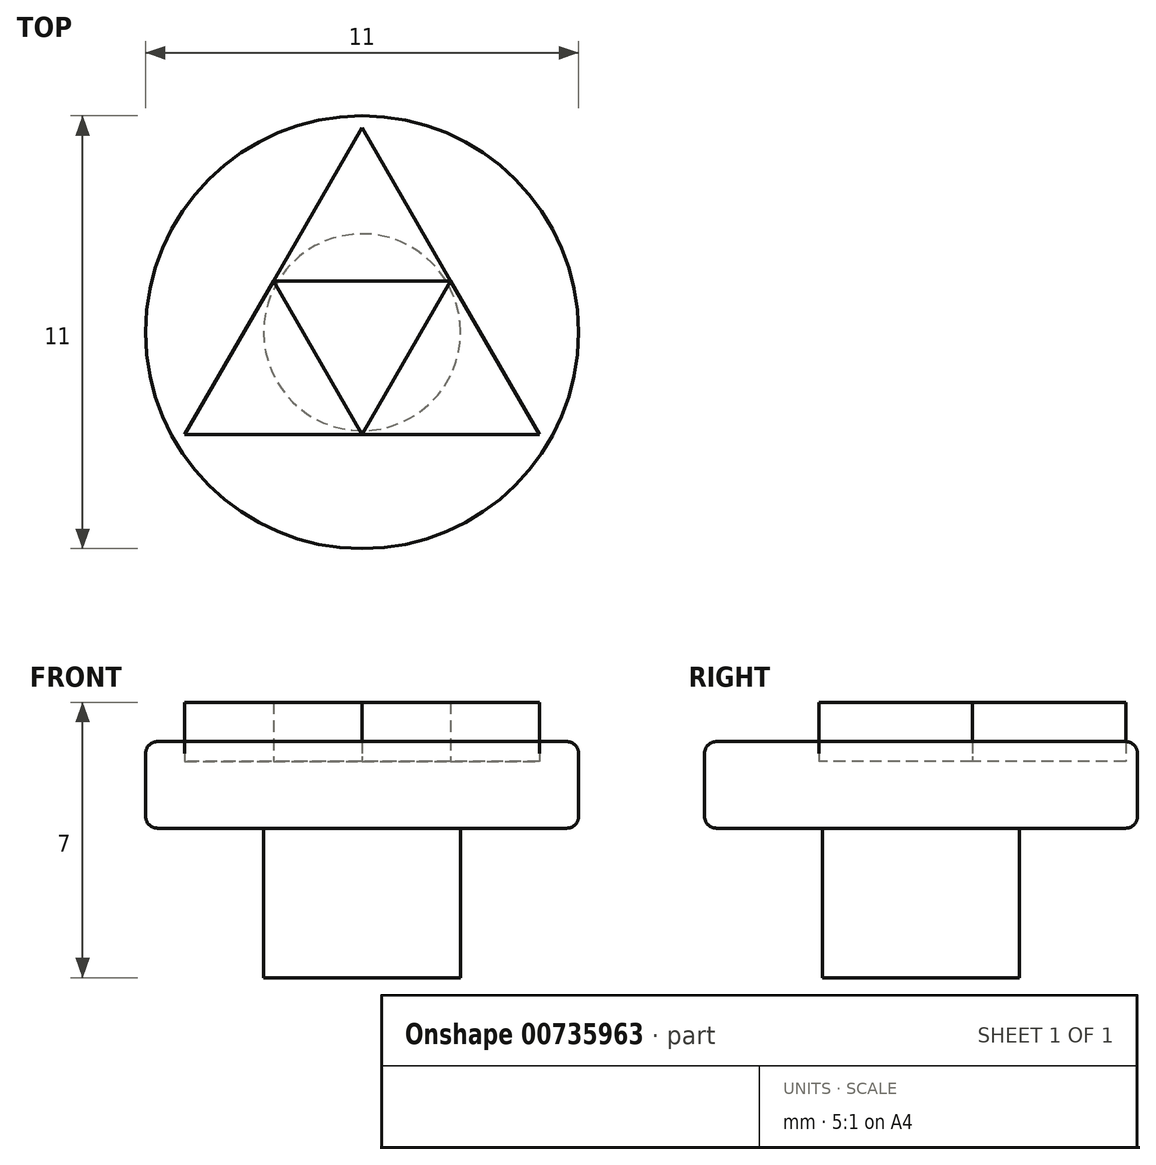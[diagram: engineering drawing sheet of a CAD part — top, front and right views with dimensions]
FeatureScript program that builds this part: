
annotation { "Feature Type Name" : "Feature", "Feature Type Description" : "" }
export const myFeature = defineFeature(function(context is Context, id is Id, definition is map)
    precondition{}
    {
        {
            var Q0;
            Q0=qCreatedBy(makeId("Front.planeOp"),FACE);
            var sketch = newSketch(context, id + "F0", { "sketchPlane" : qUnion([Q0])});
            skLineSegment(sketch, "E0.bottom", {"start": v(0, 0) * mm, "end": v(-2.5, 0) * mm});
            skLineSegment(sketch, "E0.top", {"start": v(0, 6) * mm, "end": v(-2.5, 6) * mm});
            skLineSegment(sketch, "E0.left", {"start": v(0, 0) * mm, "end": v(0, 6) * mm});
            skLineSegment(sketch, "E0.right", {"start": v(-2.5, 0) * mm, "end": v(-2.5, 6) * mm});
            skLineSegment(sketch, "E1.bottom", {"start": v(-2.5, 6) * mm, "end": v(-5.2, 6) * mm});
            skLineSegment(sketch, "E1.left", {"start": v(-2.5, 6) * mm, "end": v(-2.5, 3.8) * mm});
            skLineSegment(sketch, "E1.right", {"start": v(-5.5, 5.7) * mm, "end": v(-5.5, 4.1) * mm});
            skPoint(sketch, "E2.visualSharp", {"position": v(-5.5, 4.8) * mm});
            skArc(sketch, "E2.filletArc", {"start": v(-5.5, 4.1) * mm, "mid": v(-5.41, 3.89) * mm, "end": v(-5.2, 3.8) * mm});
            skPoint(sketch, "E3.visualSharp", {"position": v(-5.5, 6) * mm});
            skArc(sketch, "E3.filletArc", {"start": v(-5.2, 6) * mm, "mid": v(-5.41, 5.91) * mm, "end": v(-5.5, 5.7) * mm});
            skLineSegment(sketch, "E4", {"start": v(-5.2, 3.8) * mm, "end": v(-2.5, 3.8) * mm});
            skSolve(sketch);
        }
        {
            var Q0;
            {var subQ0=sQuery(id+"F0.wireOp",EDGE,"E1.bottom");var subQ6=sQuery(id+"F0.wireOp",EDGE,"E0.bottom");Q0=qUnion([makeQuery(id+"F0.imprint","IMPRINT",FACE,{"disambiguationData":[TD([[makeQuery(id+"F0.imprint","IMPRINT",EDGE,{"derivedFrom":subQ6}),-1.0]])]}),makeQuery(id+"F0.imprint","IMPRINT",FACE,{"disambiguationData":[TD([[makeQuery(id+"F0.imprint","IMPRINT",EDGE,{"derivedFrom":subQ0}),1.0]])]})]);}
            var Q1;
            Q1=sQuery(id+"F0.wireOp",EDGE,"E0.left");
            revolve(context, id + "F1", {"surfaceOperationType" : NewSurfaceOperationType.NEW, "entities" : qUnion([Q0]), "axis" : qUnion([Q1]), "revolveType" : RevolveType.FULL});
        }
        {
            var Q0;
            Q0=makeQuery(id+"F1.opRevolve","SWEPT_FACE",FACE,{"disambiguationData":[OSD([sQuery(id+"F0.wireOp",EDGE,"E0.top"),sQuery(id+"F0.wireOp",EDGE,"E1.bottom")])]});
            var sketch = newSketch(context, id + "F2", { "sketchPlane" : qUnion([Q0])});
            skCircle(sketch, "E5.cCircle", {"center": v(0, 0) * mm, "radius": 2.6 * mm, "construction": true});
            skCircle(sketch, "E6.cCircle", {"center": v(-2.25, -1.3) * mm, "radius": 2.6 * mm, "construction": true});
            skLineSegment(sketch, "E6.0", {"start": v(0, -2.6) * mm, "end": v(-4.5, -2.6) * mm});
            skLineSegment(sketch, "E6.1", {"start": v(-4.5, -2.6) * mm, "end": v(-2.25, 1.3) * mm});
            skLineSegment(sketch, "E6.2", {"start": v(-2.25, 1.3) * mm, "end": v(0, -2.6) * mm});
            skCircle(sketch, "E7.cCircle", {"center": v(0, 2.6) * mm, "radius": 2.6 * mm, "construction": true});
            skLineSegment(sketch, "E7.0", {"start": v(-2.25, 1.3) * mm, "end": v(0, 5.2) * mm});
            skLineSegment(sketch, "E7.1", {"start": v(0, 5.2) * mm, "end": v(2.25, 1.3) * mm});
            skLineSegment(sketch, "E7.2", {"start": v(2.25, 1.3) * mm, "end": v(-2.25, 1.3) * mm});
            skCircle(sketch, "E8.cCircle", {"center": v(2.25, -1.3) * mm, "radius": 2.6 * mm, "construction": true});
            skLineSegment(sketch, "E8.0", {"start": v(2.25, 1.3) * mm, "end": v(4.5, -2.6) * mm});
            skLineSegment(sketch, "E8.1", {"start": v(4.5, -2.6) * mm, "end": v(0, -2.6) * mm});
            skLineSegment(sketch, "E8.2", {"start": v(0, -2.6) * mm, "end": v(2.25, 1.3) * mm});
            skSolve(sketch);
        }
        {
            var Q0;
            {var subQ0=sQuery(id+"F2.wireOp",EDGE,"E6.2");Q0=makeQuery(id+"F2.imprint","IMPRINT",FACE,{"disambiguationData":[TD([[makeQuery(id+"F2.imprint","IMPRINT",EDGE,{"derivedFrom":subQ0}),-1.0]])]});}
            var Q1;
            {var subQ0=sQuery(id+"F2.wireOp",EDGE,"E8.2");Q1=makeQuery(id+"F2.imprint","IMPRINT",FACE,{"disambiguationData":[TD([[makeQuery(id+"F2.imprint","IMPRINT",EDGE,{"derivedFrom":subQ0}),-1.0]])]});}
            var Q2;
            {var subQ0=sQuery(id+"F2.wireOp",EDGE,"E7.2");Q2=makeQuery(id+"F2.imprint","IMPRINT",FACE,{"disambiguationData":[TD([[makeQuery(id+"F2.imprint","IMPRINT",EDGE,{"derivedFrom":subQ0}),-1.0]])]});}
            var Q3;
            {var subQ0=sQuery(id+"F2.wireOp",EDGE,"E7.1");var subQ1=sQuery(id+"F2.wireOp",EDGE,"E7.0");var subQ2=makeQuery(id+"F2.imprint","INTERSECT",VERTEX,{"derivedFrom":[subQ1,subQ0]});Q3=makeQuery(id+"F2.imprint","IMPRINT",FACE,{"disambiguationData":[TD([[makeQuery(id+"F2.imprint","IMPRINT",EDGE,{"disambiguationData":[TD([[subQ2,1.0]])],"derivedFrom":subQ1}),-1.0]])]});}
            var Q4;
            {var subQ0=sQuery(id+"F2.wireOp",EDGE,"E8.1");var subQ1=sQuery(id+"F2.wireOp",EDGE,"E8.0");var subQ2=makeQuery(id+"F2.imprint","INTERSECT",VERTEX,{"derivedFrom":[subQ1,subQ0]});Q4=makeQuery(id+"F2.imprint","IMPRINT",FACE,{"disambiguationData":[TD([[makeQuery(id+"F2.imprint","IMPRINT",EDGE,{"disambiguationData":[TD([[subQ2,1.0]])],"derivedFrom":subQ1}),-1.0]])]});}
            var Q5;
            {var subQ0=sQuery(id+"F2.wireOp",EDGE,"E6.1");var subQ1=sQuery(id+"F2.wireOp",EDGE,"E6.0");var subQ2=makeQuery(id+"F2.imprint","INTERSECT",VERTEX,{"derivedFrom":[subQ1,subQ0]});Q5=makeQuery(id+"F2.imprint","IMPRINT",FACE,{"disambiguationData":[TD([[makeQuery(id+"F2.imprint","IMPRINT",EDGE,{"disambiguationData":[TD([[subQ2,1.0]])],"derivedFrom":subQ1}),-1.0]])]});}
            extrude(context, id + "F3", {"entities" : qUnion([Q0, Q1, Q2, Q3, Q4, Q5]), "depth" : 1 * mm, "offsetDistance" : 25 * mm, "hasSecondDirection" : true, "secondDirectionOppositeDirection" : true, "secondDirectionDepth" : .5 * mm});
        }
    });
